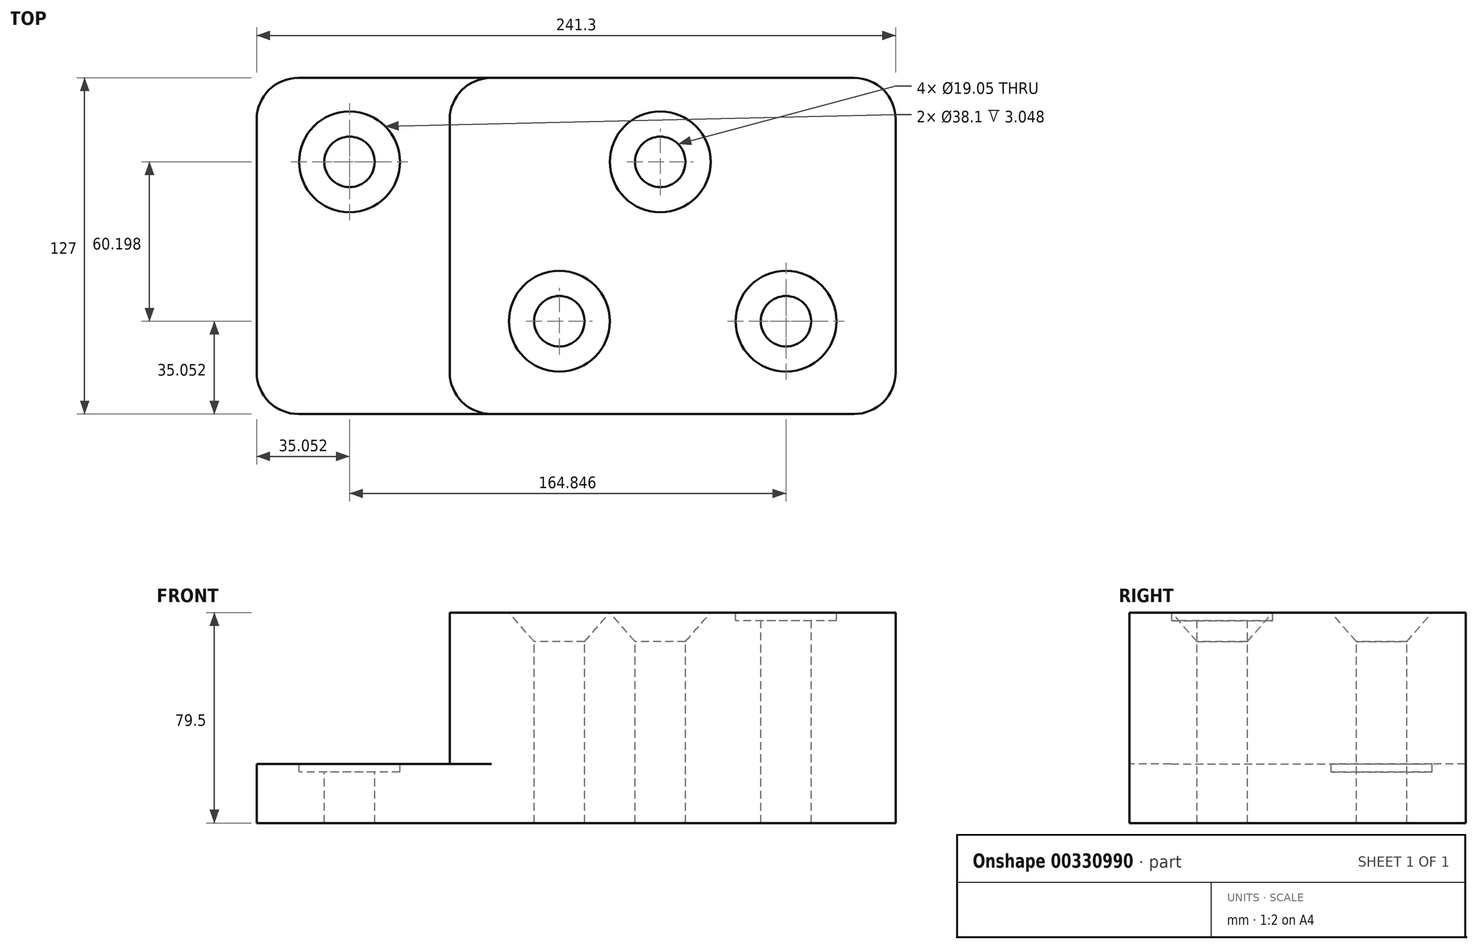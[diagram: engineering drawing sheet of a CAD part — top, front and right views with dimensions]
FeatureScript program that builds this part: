
annotation { "Feature Type Name" : "Feature", "Feature Type Description" : "" }
export const myFeature = defineFeature(function(context is Context, id is Id, definition is map)
    precondition{}
    {
        {
            var Q0;
            Q0=qCreatedBy(makeId("Top.planeOp"),FACE);
            var sketch = newSketch(context, id + "F0", { "sketchPlane" : qUnion([Q0])});
            skLineSegment(sketch, "E0", {"start": v(0, 0) * mm, "end": v(0, 127) * mm});
            skLineSegment(sketch, "E1", {"start": v(0, 127) * mm, "end": v(241.3, 127) * mm});
            skLineSegment(sketch, "E2", {"start": v(241.3, 127) * mm, "end": v(241.3, 0) * mm});
            skLineSegment(sketch, "E3", {"start": v(241.3, 0) * mm, "end": v(0, 0) * mm});
            skLineSegment(sketch, "E4", {"start": v(72.9, 127) * mm, "end": v(72.9, 0) * mm});
            skSolve(sketch);
        }
        {
            var Q0;
            {var subQ0=sQuery(id+"F0.wireOp",EDGE,"E0");Q0=makeQuery(id+"F0.imprint","IMPRINT",FACE,{"disambiguationData":[TD([[makeQuery(id+"F0.imprint","IMPRINT",EDGE,{"derivedFrom":subQ0}),-1.0]])]});}
            extrude(context, id + "F1", {"entities" : qUnion([Q0]), "depth" : 22.35 * mm});
        }
        {
            var Q0;
            {var subQ0=sQuery(id+"F0.wireOp",EDGE,"E2");Q0=makeQuery(id+"F0.imprint","IMPRINT",FACE,{"disambiguationData":[TD([[makeQuery(id+"F0.imprint","IMPRINT",EDGE,{"derivedFrom":subQ0}),-1.0]])]});}
            extrude(context, id + "F2", {"entities" : qUnion([Q0]), "operationType" : NewBodyOperationType.ADD, "depth" : 79.5 * mm});
        }
        {
            var Q0;
            Q0=makeQuery(id+"F2.opExtrude","CAP_FACE",FACE,{"disambiguationData":[OSD([sQuery(id+"F0.wireOp",EDGE,"E1"),sQuery(id+"F0.wireOp",EDGE,"E2"),sQuery(id+"F0.wireOp",EDGE,"E3"),sQuery(id+"F0.wireOp",EDGE,"E4")])],"isStart":false});
            var sketch = newSketch(context, id + "F3", { "sketchPlane" : qUnion([Q0])});
            skPoint(sketch, "E5", {"position": v(152.4, 95.25) * mm});
            skPoint(sketch, "E6", {"position": v(114.3, 35.05) * mm});
            skPoint(sketch, "E7", {"position": v(199.9, 35.05) * mm});
            skSolve(sketch);
        }
        {
            var Q0;
            Q0=makeQuery(id+"F1.opExtrude","CAP_FACE",FACE,{"disambiguationData":[OSD([sQuery(id+"F0.wireOp",EDGE,"E0"),sQuery(id+"F0.wireOp",EDGE,"E1"),sQuery(id+"F0.wireOp",EDGE,"E3"),sQuery(id+"F0.wireOp",EDGE,"E4")])],"isStart":false});
            var sketch = newSketch(context, id + "F4", { "sketchPlane" : qUnion([Q0])});
            skPoint(sketch, "E8", {"position": v(35.05, 95.25) * mm});
            skSolve(sketch);
        }
        {
            var Q0;
            Q0=sQuery(id+"F3.wireOp",VERTEX,"E7");
            var Q1;
            Q1=sQuery(id+"F4.wireOp",VERTEX,"E8");
            var Q2;
            Q2=makeQuery(id+"F1.opExtrude","SWEPT_BODY",BODY,{"disambiguationData":[OSD([sQuery(id+"F0.wireOp",EDGE,"E0"),sQuery(id+"F0.wireOp",EDGE,"E1"),sQuery(id+"F0.wireOp",EDGE,"E3"),sQuery(id+"F0.wireOp",EDGE,"E4")])]});
            hole(context, id + "F5", {"style" : HoleStyle.C_BORE, "endStyle" : HoleEndStyle.THROUGH, "holeDiameter" : 19.05 * mm, "cBoreDiameter" : 38.1 * mm, "cBoreDepth" : 3.05 * mm, "tappedDepth" : 12.7 * mm, "tapClearance" : 3, "locations" : qUnion([Q0, Q1]), "scope" : qUnion([Q2])});
        }
        {
            var Q0;
            Q0=sQuery(id+"F3.wireOp",VERTEX,"E5");
            var Q1;
            Q1=sQuery(id+"F3.wireOp",VERTEX,"E6");
            var Q2;
            Q2=makeQuery(id+"F1.opExtrude","SWEPT_BODY",BODY,{"disambiguationData":[OSD([sQuery(id+"F0.wireOp",EDGE,"E0"),sQuery(id+"F0.wireOp",EDGE,"E1"),sQuery(id+"F0.wireOp",EDGE,"E3"),sQuery(id+"F0.wireOp",EDGE,"E4")])]});
            hole(context, id + "F6", {"style" : HoleStyle.C_SINK, "endStyle" : HoleEndStyle.THROUGH, "holeDiameter" : 19.05 * mm, "cSinkDiameter" : 38.1 * mm, "cSinkAngle" : 82 * degree, "tappedDepth" : 12.7 * mm, "tapClearance" : 3, "locations" : qUnion([Q0, Q1]), "scope" : qUnion([Q2])});
        }
        {
            var Q0;
            Q0=makeQuery(id+"F2.opExtrude","SWEPT_EDGE",EDGE,{"disambiguationData":[OSD([sQuery(id+"F0.wireOp",EDGE,"E3"),sQuery(id+"F0.wireOp",EDGE,"E4")])]});
            var Q1;
            Q1=makeQuery(id+"F2.opExtrude","SWEPT_EDGE",EDGE,{"disambiguationData":[OSD([sQuery(id+"F0.wireOp",EDGE,"E2"),sQuery(id+"F0.wireOp",EDGE,"E3")])]});
            var Q2;
            Q2=makeQuery(id+"F2.opExtrude","SWEPT_EDGE",EDGE,{"disambiguationData":[OSD([sQuery(id+"F0.wireOp",EDGE,"E1"),sQuery(id+"F0.wireOp",EDGE,"E2")])]});
            var Q3;
            Q3=makeQuery(id+"F2.opExtrude","SWEPT_EDGE",EDGE,{"disambiguationData":[OSD([sQuery(id+"F0.wireOp",EDGE,"E1"),sQuery(id+"F0.wireOp",EDGE,"E4")])]});
            var Q4;
            Q4=makeQuery(id+"F1.opExtrude","SWEPT_EDGE",EDGE,{"disambiguationData":[OSD([sQuery(id+"F0.wireOp",EDGE,"E0"),sQuery(id+"F0.wireOp",EDGE,"E1")])]});
            var Q5;
            Q5=makeQuery(id+"F1.opExtrude","SWEPT_EDGE",EDGE,{"disambiguationData":[OSD([sQuery(id+"F0.wireOp",EDGE,"E0"),sQuery(id+"F0.wireOp",EDGE,"E3")])]});
            fillet(context, id + "F7", {"entities" : qUnion([Q0, Q1, Q2, Q3, Q4, Q5]), "radius" : 15.75 * mm, "tangentPropagation" : true, "allowEdgeOverflow" : false});
        }
    });
